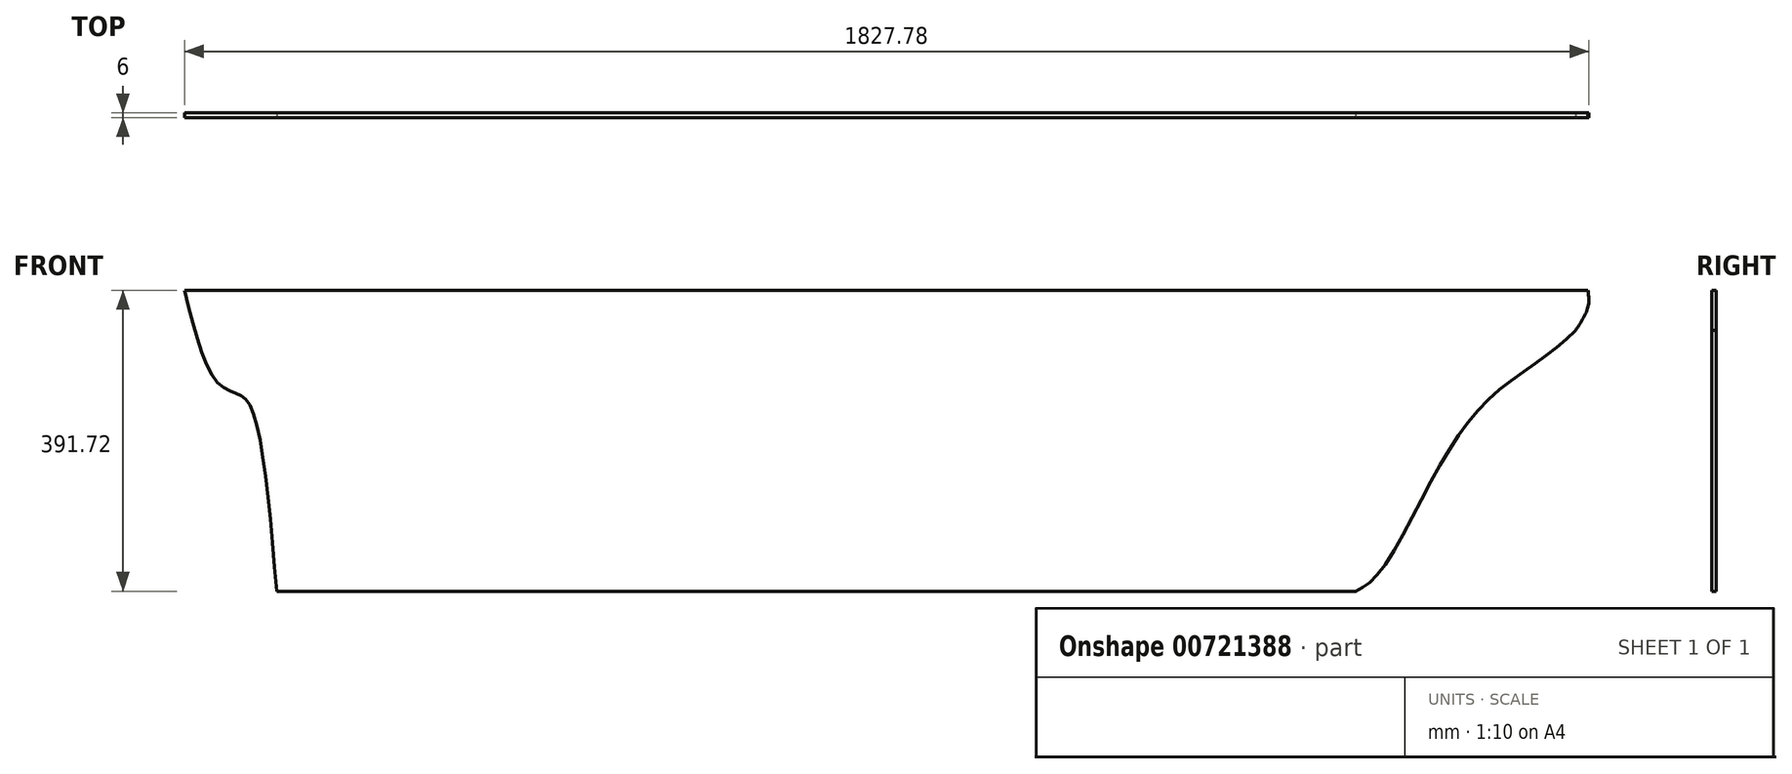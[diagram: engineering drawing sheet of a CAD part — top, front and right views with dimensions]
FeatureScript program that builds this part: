
annotation { "Feature Type Name" : "Feature", "Feature Type Description" : "" }
export const myFeature = defineFeature(function(context is Context, id is Id, definition is map)
    precondition{}
    {
        {
            var Q0;
            Q0=qCreatedBy(makeId("Front.planeOp"),FACE);
            var sketch = newSketch(context, id + "F0", { "sketchPlane" : qUnion([Q0])});
            skLineSegment(sketch, "E0", {"start": v(0, 0) * mm, "end": v(795.18, 0) * mm, "construction": true});
            skLineSegment(sketch, "E1", {"start": v(0, 0) * mm, "end": v(-1236.83, 0) * mm, "construction": true});
            skLineSegment(sketch, "E2", {"start": v(0, 0) * mm, "end": v(0, 322.32) * mm, "construction": true});
            skLineSegment(sketch, "E3", {"start": v(0, 0) * mm, "end": v(0, -474.6) * mm, "construction": true});
            skLineSegment(sketch, "E4", {"start": v(-6, -186.98) * mm, "end": v(-6, 169.17) * mm, "construction": true});
            skSolve(sketch);
        }
        {
            var Q0;
            Q0=qCreatedBy(makeId("Front.planeOp"),FACE);
            var sketch = newSketch(context, id + "F1", { "sketchPlane" : qUnion([Q0])});
            skFitSpline(sketch, "E5", {"points": [v(-1073.86, 212.04) * mm, v(-1031.52, 92.77) * mm, v(-1004.68, 77.27) * mm, v(-986.2, 57.59) * mm, v(-953.7, -179.68) * mm], "startDerivative": vector(123.45, -498.41) * mm, "endDerivative": vector(62.84, -733.7) * mm});
            skLineSegment(sketch, "E6", {"start": v(-953.7, -179.68) * mm, "end": v(450.42, -179.68) * mm});
            skFitSpline(sketch, "E7", {"points": [v(752.79, 175.25) * mm, v(699.63, 128.11) * mm, v(624.41, 70.95) * mm, v(553.2, -28.34) * mm, v(479.99, -156.72) * mm, v(450.42, -179.68) * mm], "startDerivative": vector(-278.65, -268.34) * mm, "endDerivative": vector(-218.9, -116.73) * mm});
            skLineSegment(sketch, "E8", {"start": v(-1073.86, 212.04) * mm, "end": v(752.79, 212.04) * mm});
            skFitSpline(sketch, "E9", {"points": [v(752.79, 212.04) * mm, v(752.79, 189.84) * mm, v(736.3, 159.37) * mm], "startDerivative": vector(6.6, -48.83) * mm, "endDerivative": vector(-37.93, -56.23) * mm});
            skSolve(sketch);
        }
        {
            var Q0;
            Q0=makeQuery(id+"F1.imprint","IMPRINT",FACE,{"disambiguationData":[TD([[makeQuery(id+"F1.imprint","IMPRINT",EDGE,{"derivedFrom":sQuery(id+"F1.wireOp",EDGE,"E5")}),1.0]])]});
            extrude(context, id + "F2", {"entities" : qUnion([Q0]), "oppositeDirection" : true, "depth" : 6 * mm, "offsetDistance" : 25 * mm});
        }
    });
